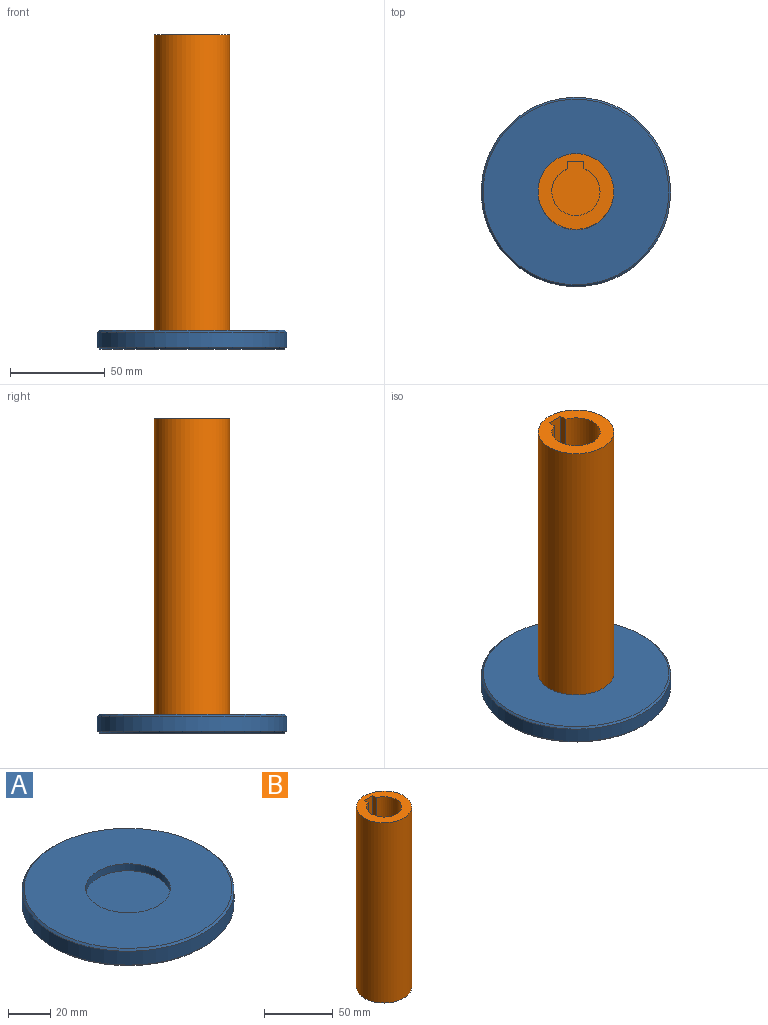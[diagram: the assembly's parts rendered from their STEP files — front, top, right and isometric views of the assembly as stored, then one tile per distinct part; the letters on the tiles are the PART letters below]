
ASSEMBLY  parts=2 mates=2
PART A: 7 faces, bbox 100x100x10 mm
  f0: cylinder r=50mm len=100mm, axis (0,0,-1), area 2513.3mm2, adj f5,f6
  f1: plane 98x98mm, normal (0,0,1), area 6286.3mm2, adj f3,f6
  f2: plane 98x98mm, normal (0,0,-1), area 7543mm2, adj f5
  f3: cylinder r=20mm len=40mm, axis (0,0,1), area 502.7mm2, adj f1,f4
  f4: plane 40x40mm, normal (0,0,1), area 1256.6mm2, adj f3
  f5: cone r=50mm half-angle=45deg, axis (0,0,1), area 439.8mm2, adj f0,f2
  f6: cone r=49mm half-angle=45deg, axis (0,0,-1), area 439.8mm2, adj f0,f1
PART B: 8 faces, bbox 40x40x160 mm
  f0: cylinder r=20mm len=160mm, axis (0,0,-1), area 20106.2mm2, adj f1,f2
  f1: plane 40x40mm, normal (0,0,1), area 718.4mm2, adj f0,f3,f4,f5,f6
  f2: plane 40x40mm, normal (0,0,-1), area 1256.6mm2, adj f0
  f3: plane 50x3.73mm, normal (1,0,0), area 186.5mm2, adj f1,f4,f6,f7
  f4: cylinder r=12.75mm len=50mm, axis (0,0,1), area 3572.2mm2, adj f1,f3,f5,f7
  f5: plane 50x3.73mm, normal (-1,0,0), area 186.5mm2, adj f1,f4,f6,f7
  f6: plane 50x8.5mm, normal (0,-1,0), area 425mm2, adj f1,f3,f5,f7
  f7: plane 28.5x25.5mm, normal (0,0,1), area 538.2mm2, adj f3,f4,f5,f6
PLACE A at identity
PLACE B t=(0,0,6)mm
MATE planar B.f0 <-> A.f3  axis (0,0,-1) through (0,0,6)mm
MATE cylindrical B.f0 <-> A.f3  axis (0,0,-1) through (0,0,6)mm
